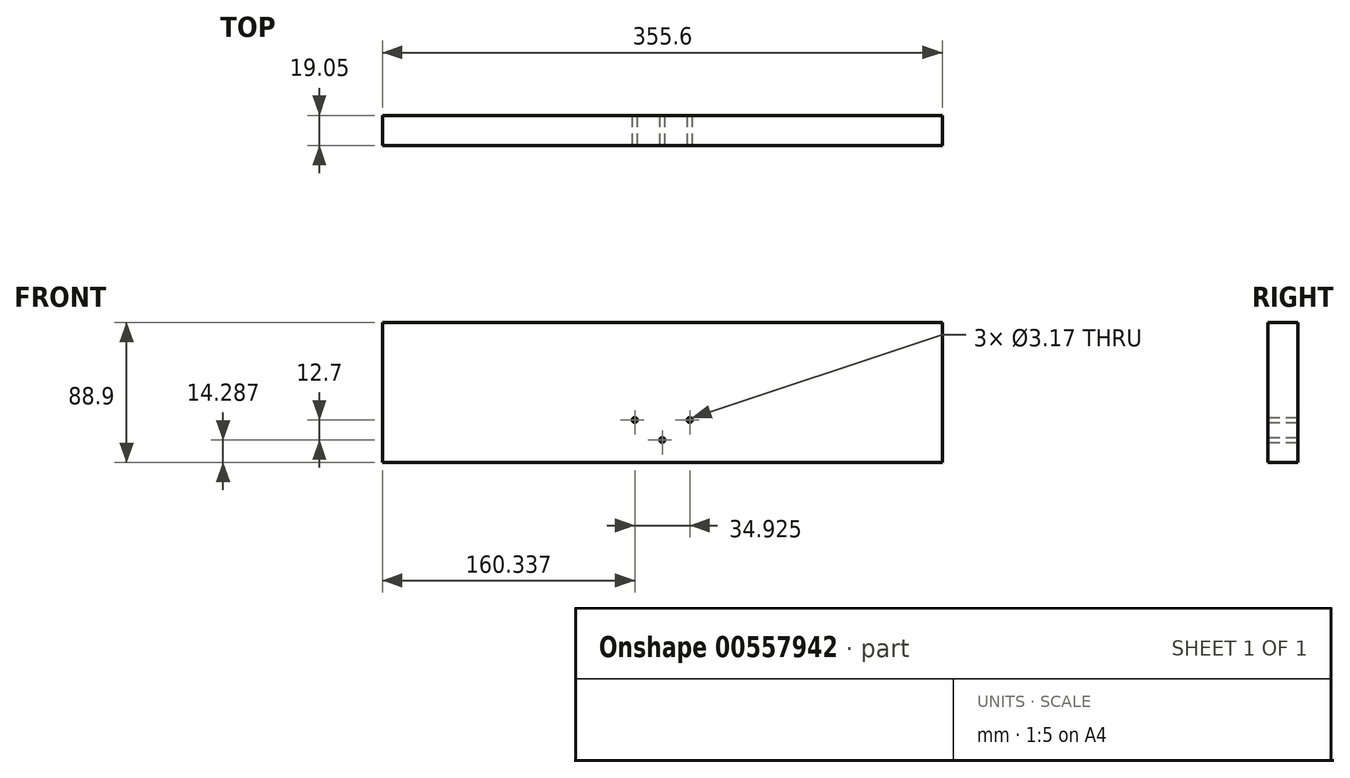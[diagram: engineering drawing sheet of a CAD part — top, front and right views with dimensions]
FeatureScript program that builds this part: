
annotation { "Feature Type Name" : "Feature", "Feature Type Description" : "" }
export const myFeature = defineFeature(function(context is Context, id is Id, definition is map)
    precondition{}
    {
        {
            var Q0;
            Q0=qCreatedBy(makeId("Front.planeOp"),FACE);
            var sketch = newSketch(context, id + "F0", { "sketchPlane" : qUnion([Q0])});
            skLineSegment(sketch, "E0.bottom", {"start": v(378.46, 16.51) * mm, "end": v(22.86, 16.51) * mm});
            skLineSegment(sketch, "E0.top", {"start": v(378.46, 105.41) * mm, "end": v(22.86, 105.41) * mm});
            skPoint(sketch, "E0.middle", {"position": v(200.66, 60.96) * mm});
            skLineSegment(sketch, "E1", {"start": v(22.86, 105.41) * mm, "end": v(22.86, 16.51) * mm});
            skLineSegment(sketch, "E2", {"start": v(378.46, 105.41) * mm, "end": v(378.46, 16.51) * mm});
            skCircle(sketch, "E3", {"center": v(200.66, 30.8) * mm, "radius": 1.59 * mm});
            skCircle(sketch, "E4", {"center": v(218.12, 43.5) * mm, "radius": 1.59 * mm});
            skCircle(sketch, "E5", {"center": v(183.2, 43.5) * mm, "radius": 1.59 * mm});
            skSolve(sketch);
        }
        {
            var Q0;
            Q0=makeQuery(id+"F0.imprint","IMPRINT",FACE,{"disambiguationData":[TD([[makeQuery(id+"F0.imprint","IMPRINT",EDGE,{"derivedFrom":sQuery(id+"F0.wireOp",EDGE,"E0.bottom")}),-1.0]])]});
            extrude(context, id + "F1", {"entities" : qUnion([Q0]), "depth" : 19.05 * mm, "offsetDistance" : 25.4 * mm});
        }
    });
